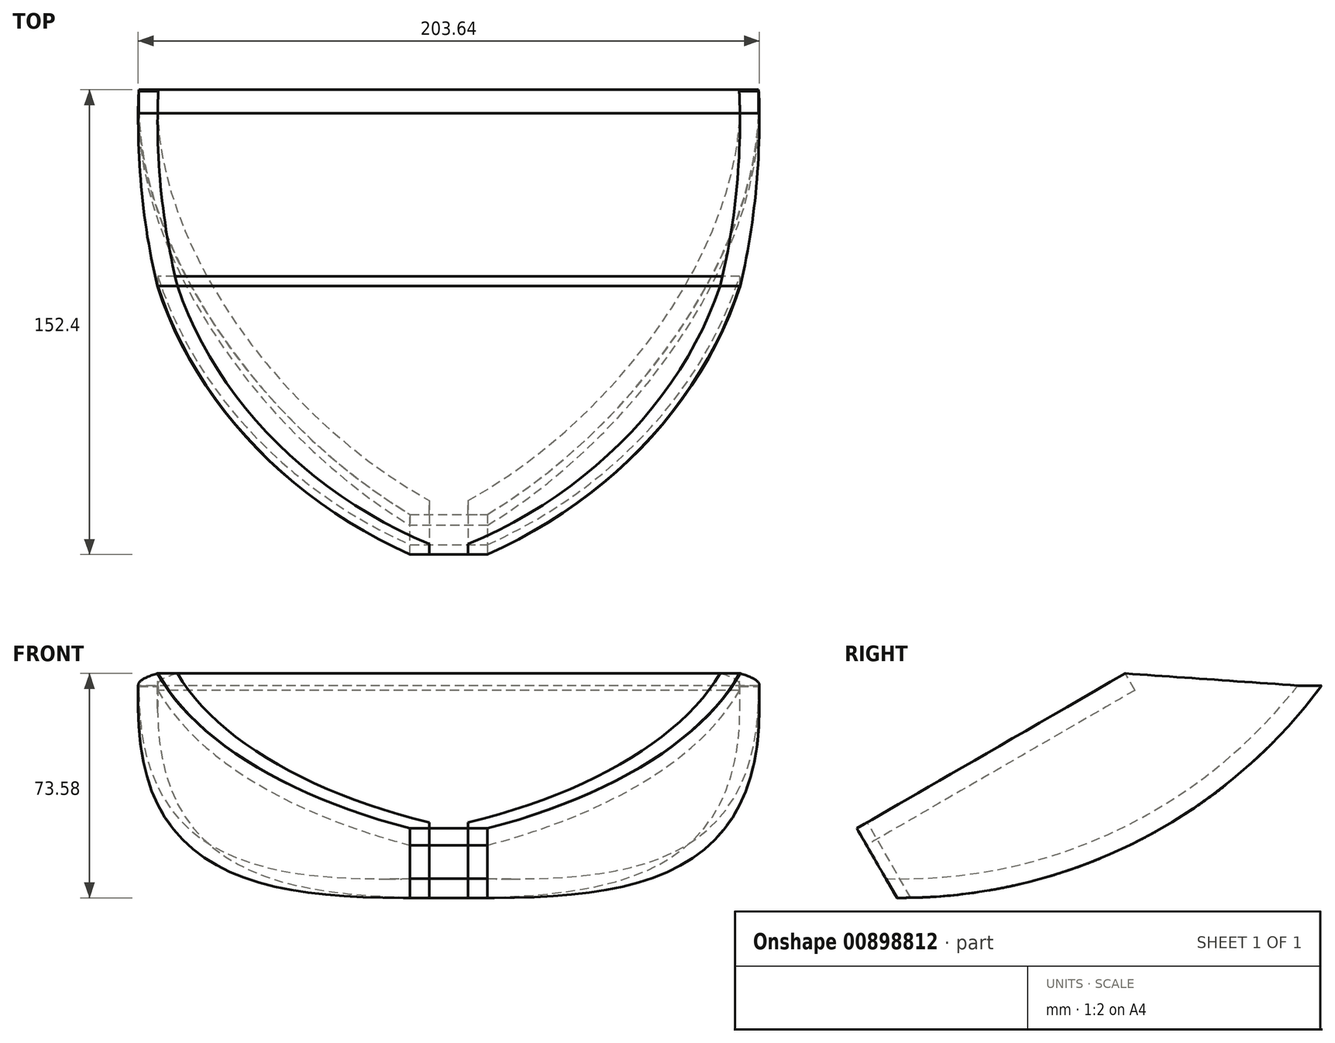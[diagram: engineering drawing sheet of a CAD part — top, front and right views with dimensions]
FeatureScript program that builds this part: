
annotation { "Feature Type Name" : "Feature", "Feature Type Description" : "" }
export const myFeature = defineFeature(function(context is Context, id is Id, definition is map)
    precondition{}
    {
        {
            var Q0;
            Q0=qCreatedBy(makeId("Right.planeOp"),FACE);
            var sketch = newSketch(context, id + "F0", { "sketchPlane" : qUnion([Q0])});
            skArc(sketch, "E0", {"start": v(-43.6, -47.1) * mm, "mid": v(34.4, -29.02) * mm, "end": v(95.66, 22.5) * mm});
            skArc(sketch, "E1", {"start": v(-47.21, -40.82) * mm, "mid": v(27.9, -25.29) * mm, "end": v(87.88, 22.5) * mm});
            skLineSegment(sketch, "E2", {"start": v(87.88, 22.5) * mm, "end": v(95.66, 22.5) * mm});
            skLineSegment(sketch, "E3", {"start": v(-53.56, -29.82) * mm, "end": v(34.43, 20.98) * mm});
            skLineSegment(sketch, "E4", {"start": v(-56.74, -24.32) * mm, "end": v(31.25, 26.48) * mm});
            skLineSegment(sketch, "E5", {"start": v(-56.74, -24.32) * mm, "end": v(-53.56, -29.82) * mm});
            skLineSegment(sketch, "E6", {"start": v(31.25, 26.48) * mm, "end": v(34.43, 20.98) * mm});
            skPoint(sketch, "E7.end.orphan", {"position": v(37.08, 22.5) * mm});
            skPoint(sketch, "E8.start.orphan", {"position": v(-58.09, -32.43) * mm});
            skPoint(sketch, "E9.start.orphan", {"position": v(-58.09, -40.13) * mm});
            skPoint(sketch, "E10.orphan", {"position": v(-56.74, -46.48) * mm});
            skLineSegment(sketch, "E11.trimOffspring", {"start": v(-47.21, -40.82) * mm, "end": v(-43.6, -47.1) * mm});
            skSolve(sketch);
        }
        {
            var Q0;
            Q0 = qSketchRegion(id + "F0", true);
            extrude(context, id + "F1", {"entities" : qUnion([Q0]), "depth" : 101.6 * mm, "offsetDistance" : 25.4 * mm, "hasSecondDirection" : true, "secondDirectionOppositeDirection" : true, "secondDirectionDepth" : 101.6 * mm});
        }
        {
            var Q0;
            Q0=makeQuery(id+"F1.opExtrude","SWEPT_FACE",FACE,{"disambiguationData":[OSD([sQuery(id+"F0.wireOp",EDGE,"E4")])]});
            var sketch = newSketch(context, id + "F2", { "sketchPlane" : qUnion([Q0])});
            skArc(sketch, "E12", {"start": v(-101.6, 85.61) * mm, "mid": v(-77.75, -0.3) * mm, "end": v(-12.7, -61.3) * mm});
            skLineSegment(sketch, "E13", {"start": v(-101.6, 85.61) * mm, "end": v(-101.6, -61.3) * mm});
            skLineSegment(sketch, "E14", {"start": v(-101.6, -61.3) * mm, "end": v(-12.7, -61.3) * mm});
            skArc(sketch, "E15.MirrorCS", {"start": v(101.6, 85.61) * mm, "mid": v(77.75, -0.3) * mm, "end": v(12.7, -61.3) * mm});
            skLineSegment(sketch, "E16.MirrorCS", {"start": v(101.6, 85.61) * mm, "end": v(101.6, -61.3) * mm});
            skLineSegment(sketch, "E17.MirrorCS", {"start": v(101.6, -61.3) * mm, "end": v(12.7, -61.3) * mm});
            skSolve(sketch);
        }
        {
            var Q0;
            Q0 = qSketchRegion(id + "F2", true);
            extrude(context, id + "F3", {"entities" : qUnion([Q0]), "operationType" : NewBodyOperationType.REMOVE, "oppositeDirection" : true, "depth" : 63 * mm, "offsetDistance" : 25.4 * mm});
        }
        {
            var Q0;
            Q0=makeQuery(id+"F1.opExtrude","SWEPT_FACE",FACE,{"disambiguationData":[OSD([sQuery(id+"F0.wireOp",EDGE,"E4")])]});
            var sketch = newSketch(context, id + "F4", { "sketchPlane" : qUnion([Q0])});
            skArc(sketch, "E18", {"start": v(-101.6, 93.7) * mm, "mid": v(-79.93, 3.14) * mm, "end": v(-12.7, -61.3) * mm});
            skArc(sketch, "E19.0", {"start": v(-95.24, 93.7) * mm, "mid": v(-73.54, 4.78) * mm, "end": v(-6.35, -57.38) * mm});
            skLineSegment(sketch, "E20", {"start": v(-12.7, -61.3) * mm, "end": v(-6.35, -61.3) * mm});
            skLineSegment(sketch, "E21", {"start": v(-6.35, -61.3) * mm, "end": v(-6.35, -57.38) * mm});
            skLineSegment(sketch, "E22", {"start": v(-101.6, 93.7) * mm, "end": v(-95.24, 93.7) * mm});
            skLineSegment(sketch, "E23.MirrorCS", {"start": v(12.7, -61.3) * mm, "end": v(6.35, -61.3) * mm});
            skLineSegment(sketch, "E24.MirrorCS", {"start": v(101.6, 93.7) * mm, "end": v(95.24, 93.7) * mm});
            skLineSegment(sketch, "E25.MirrorCS", {"start": v(6.35, -61.3) * mm, "end": v(6.35, -57.38) * mm});
            skArc(sketch, "E26.MirrorCS", {"start": v(101.6, 93.7) * mm, "mid": v(79.93, 3.14) * mm, "end": v(12.7, -61.3) * mm});
            skArc(sketch, "E27.MirrorCS", {"start": v(95.24, 93.7) * mm, "mid": v(73.54, 4.78) * mm, "end": v(6.35, -57.38) * mm});
            skSolve(sketch);
        }
        {
            var Q0;
            Q0 = qSketchRegion(id + "F4", true);
            extrude(context, id + "F5", {"entities" : qUnion([Q0]), "oppositeDirection" : true, "depth" : 50.8 * mm, "offsetDistance" : 25.4 * mm});
        }
        {
            var Q0;
            Q0=qCreatedBy(makeId("Right.planeOp"),FACE);
            var sketch = newSketch(context, id + "F6", { "sketchPlane" : qUnion([Q0])});
            skLineSegment(sketch, "E28", {"start": v(31.25, 26.48) * mm, "end": v(87.87, 22.5) * mm});
            skLineSegment(sketch, "E29", {"start": v(87.87, 22.5) * mm, "end": v(95.66, 22.5) * mm});
            skLineSegment(sketch, "E30", {"start": v(31.25, 26.48) * mm, "end": v(-56.74, -24.32) * mm});
            skLineSegment(sketch, "E31", {"start": v(-56.74, -24.32) * mm, "end": v(-43.6, -47.1) * mm});
            skArc(sketch, "E32", {"start": v(-43.6, -47.1) * mm, "mid": v(34.4, -29.01) * mm, "end": v(95.66, 22.5) * mm});
            skLineSegment(sketch, "E33.bottom", {"start": v(-91.5, 69.16) * mm, "end": v(126.55, 69.16) * mm});
            skLineSegment(sketch, "E33.top", {"start": v(-91.5, -73.06) * mm, "end": v(126.55, -73.06) * mm});
            skLineSegment(sketch, "E33.left", {"start": v(-91.5, 69.16) * mm, "end": v(-91.5, -73.06) * mm});
            skLineSegment(sketch, "E33.right", {"start": v(126.55, 69.16) * mm, "end": v(126.55, -73.06) * mm});
            skSolve(sketch);
        }
        {
            var Q0;
            Q0 = qSketchRegion(id + "F6", true);
            extrude(context, id + "F7", {"entities" : qUnion([Q0]), "operationType" : NewBodyOperationType.REMOVE, "oppositeDirection" : true, "depth" : 109.22 * mm, "offsetDistance" : 25.4 * mm, "hasSecondDirection" : true, "secondDirectionOppositeDirection" : false, "secondDirectionDepth" : 114.3 * mm});
        }
    });
